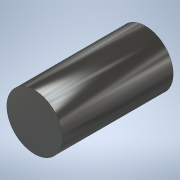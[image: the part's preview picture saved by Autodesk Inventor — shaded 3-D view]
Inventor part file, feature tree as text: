
AUTODESK INVENTOR PART (.ipt)
format: ipt  version: 2021 (Build 250183000, 183)  size: 100,864 bytes
history: native  units: in
note: dims shown in document units (in); Inventor stores cm internally (conversion verified against a paired STEP export)
features: extrude x1, sketch x1
ambient origin geometry x8: Origin, YZ Plane, XZ Plane, XY Plane, X Axis, Y Axis, Z Axis, Center Point
bodies: Solid1 (feature_tree)
feature tree (2):
  extrude  "Extrusion1"  Depth=0.1575in TaperAngle=0.0deg
  sketch  "Sketch1"  dims[d0=0.0787in d1=0.1575in d2=0.0in]
